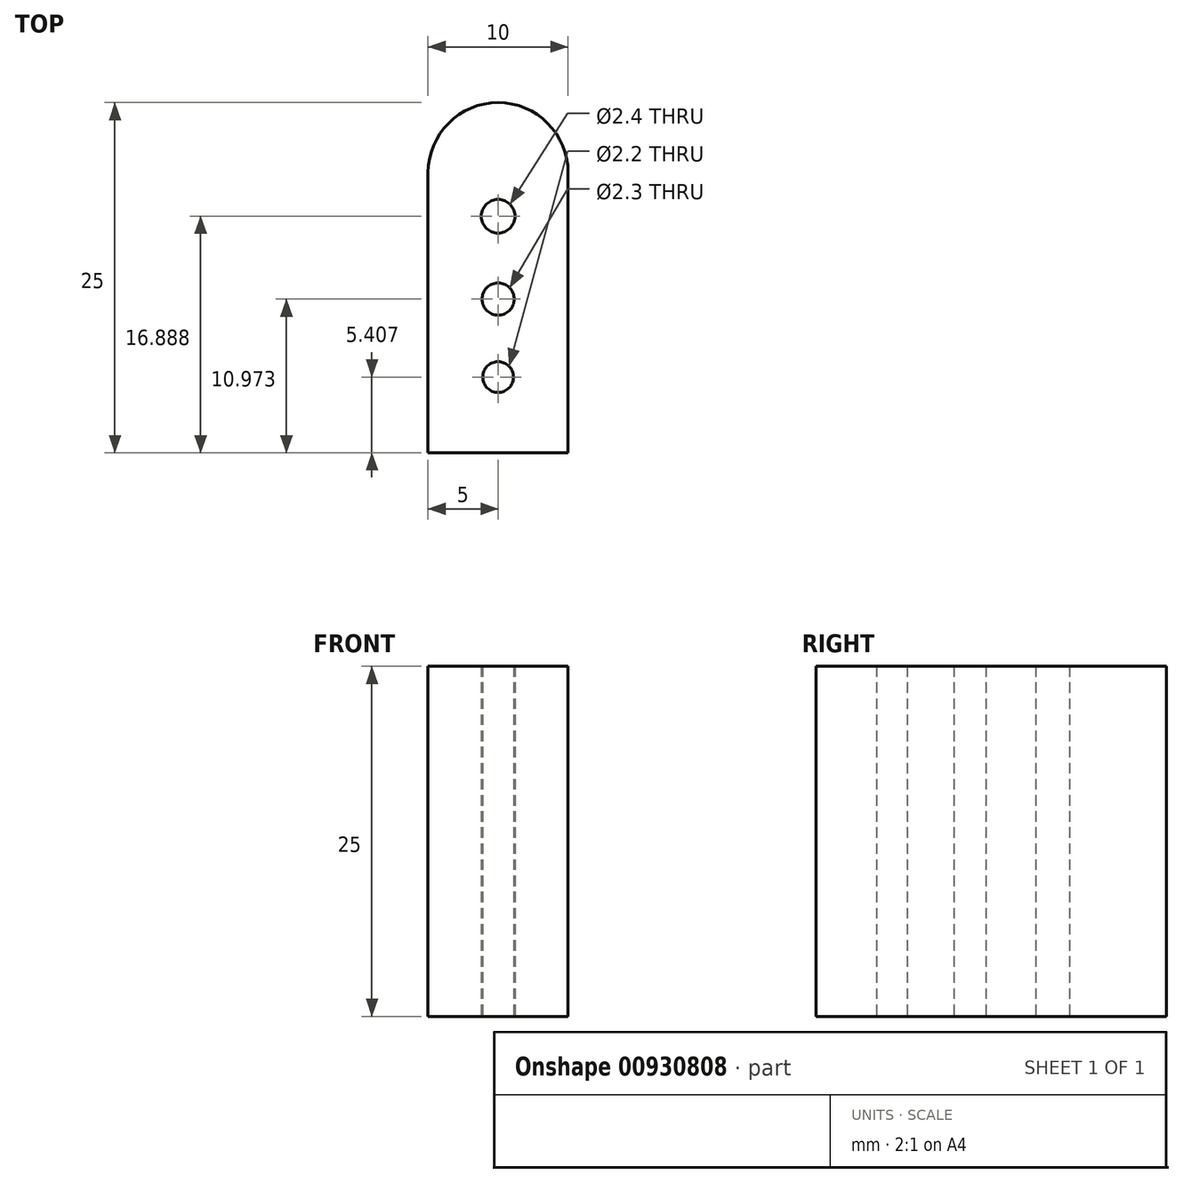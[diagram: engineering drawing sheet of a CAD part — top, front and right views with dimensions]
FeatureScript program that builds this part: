
annotation { "Feature Type Name" : "Feature", "Feature Type Description" : "" }
export const myFeature = defineFeature(function(context is Context, id is Id, definition is map)
    precondition{}
    {
        {
            var Q0;
            Q0=qCreatedBy(makeId("Top.planeOp"),FACE);
            var sketch = newSketch(context, id + "F0", { "sketchPlane" : qUnion([Q0])});
            skLineSegment(sketch, "E0.bottom", {"start": v(-10, 34.34) * mm, "end": v(-10, 34.34) * mm});
            skLineSegment(sketch, "E0.top", {"start": v(-15, 9.34) * mm, "end": v(-5, 9.34) * mm});
            skLineSegment(sketch, "E0.left", {"start": v(-15, 29.34) * mm, "end": v(-15, 9.34) * mm});
            skLineSegment(sketch, "E0.right", {"start": v(-5, 29.34) * mm, "end": v(-5, 9.34) * mm});
            skPoint(sketch, "E1.visualSharp", {"position": v(-15, 34.34) * mm});
            skArc(sketch, "E1.filletArc", {"start": v(-10, 34.34) * mm, "mid": v(-13.54, 32.88) * mm, "end": v(-15, 29.34) * mm});
            skPoint(sketch, "E2.visualSharp", {"position": v(-5, 34.34) * mm});
            skArc(sketch, "E2.filletArc", {"start": v(-5, 29.34) * mm, "mid": v(-6.46, 32.88) * mm, "end": v(-10, 34.34) * mm});
            skLineSegment(sketch, "E3", {"start": v(-10, 34.34) * mm, "end": v(-10, 9.34) * mm, "construction": true});
            skCircle(sketch, "E4", {"center": v(-10, 26.23) * mm, "radius": 1.2 * mm});
            skCircle(sketch, "E5", {"center": v(-10, 14.75) * mm, "radius": 1.1 * mm});
            skCircle(sketch, "E6", {"center": v(-10, 20.31) * mm, "radius": 1.15 * mm});
            skSolve(sketch);
        }
        {
            var Q0;
            Q0=makeQuery(id+"F0.imprint","IMPRINT",FACE,{"disambiguationData":[TD([[makeQuery(id+"F0.imprint","IMPRINT",EDGE,{"derivedFrom":sQuery(id+"F0.wireOp",EDGE,"E0.top")}),1.0]])]});
            extrude(context, id + "F1", {"entities" : qUnion([Q0]), "depth" : 25 * mm, "offsetDistance" : 25 * mm});
        }
    });
